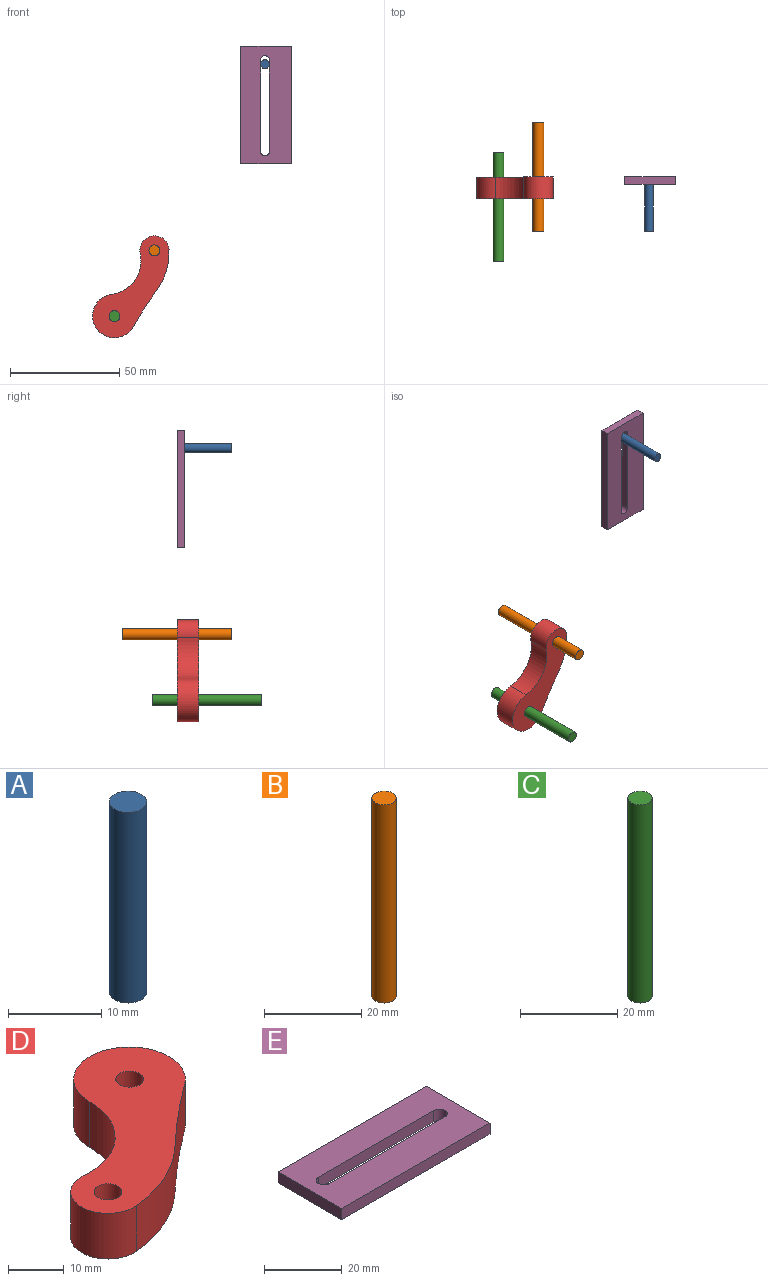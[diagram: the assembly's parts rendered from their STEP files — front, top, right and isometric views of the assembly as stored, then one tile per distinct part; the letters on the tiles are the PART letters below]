
ASSEMBLY  parts=5 mates=4
PART A: 3 faces, bbox 4x4x25 mm
  f0: cylinder r=2mm len=25mm, axis (0,0,-1), area 314.2mm2, adj f1,f2
  f1: plane 4x4mm, normal (0,0,1), area 12.6mm2, adj f0
  f2: plane 4x4mm, normal (0,0,-1), area 12.6mm2, adj f0
PART B: 3 faces, bbox 5x5x50 mm
  f0: cylinder r=2.5mm len=50mm, axis (0,0,-1), area 785.4mm2, adj f1,f2
  f1: plane 5x5mm, normal (0,0,1), area 19.6mm2, adj f0
  f2: plane 5x5mm, normal (0,0,-1), area 19.6mm2, adj f0
PART C: 3 faces, bbox 5x5x50 mm
  f0: cylinder r=2.5mm len=50mm, axis (0,0,-1), area 785.4mm2, adj f1,f2
  f1: plane 5x5mm, normal (0,0,1), area 19.6mm2, adj f0
  f2: plane 5x5mm, normal (0,0,-1), area 19.6mm2, adj f0
PART D: 9 faces, bbox 44.1x38.7x10 mm
  f0: cylinder r=10mm len=20mm, axis (0,0,-1), area 408.1mm2, adj f1,f5,f7,f8
  f1: cylinder r=15.41mm len=16.82mm, axis (0,0,-1), area 256.1mm2, adj f0,f2,f7,f8
  f2: cylinder r=6.67mm len=13.34mm, axis (0,0,-1), area 221.8mm2, adj f1,f3,f7,f8
  f3: cylinder r=29.75mm len=17.8mm, axis (0,0,-1), area 199.1mm2, adj f2,f5,f7,f8
  f4: cylinder r=2.5mm len=10mm, axis (0,0,-1), area 157.1mm2, adj f7,f8
  f5: cylinder r=150.72mm len=14.93mm, axis (0,0,-1), area 194.7mm2, adj f0,f3,f7,f8
  f6: cylinder r=2.5mm len=10mm, axis (0,0,-1), area 157.1mm2, adj f7,f8
  f7: plane 44.1x38.66mm, normal (0,0,1), area 679.5mm2, adj f0,f1,f2,f3,f4,f5,f6
  f8: plane 44.1x38.66mm, normal (0,0,-1), area 679.5mm2, adj f0,f1,f2,f3,f4,f5,f6
PART E: 10 faces, bbox 53.9x23.1x3.5 mm
  f0: cylinder r=2mm len=4mm, axis (0,0,-1), area 22mm2, adj f1,f7,f8,f9
  f1: plane 41.94x3.5mm, normal (0,-1,0), area 146.8mm2, adj f0,f2,f8,f9
  f2: cylinder r=2mm len=4mm, axis (0,0,-1), area 22mm2, adj f1,f7,f8,f9
  f3: plane 53.89x3.5mm, normal (0,1,0), area 188.6mm2, adj f4,f6,f8,f9
  f4: plane 23.14x3.5mm, normal (-1,0,0), area 81mm2, adj f3,f5,f8,f9
  f5: plane 53.89x3.5mm, normal (0,-1,0), area 188.6mm2, adj f4,f6,f8,f9
  f6: plane 23.14x3.5mm, normal (1,0,0), area 81mm2, adj f3,f5,f8,f9
  f7: plane 41.94x3.5mm, normal (0,1,0), area 146.8mm2, adj f0,f2,f8,f9
  f8: plane 53.89x23.14mm, normal (0,0,1), area 1066.7mm2, adj f0,f1,f2,f3,f4,f5,f6,f7
  f9: plane 53.89x23.14mm, normal (0,0,-1), area 1066.7mm2, adj f0,f1,f2,f3,f4,f5,f6,f7
PLACE A rot(axis=(0.96,-0.19,0.19),92.3deg) t=(50.7,0,97.99)mm
PLACE B rot(axis=(-0.47,0.62,0.62),129.6deg) t=(1.64,-10,-2.36)mm
PLACE C rot(axis=(-0.63,0.55,0.55),115.9deg) t=(5.88,-23.69,-31.31)mm
PLACE D rot(axis=(-0.63,0.55,0.55),115.9deg) t=(-0.01,-10,0.04)mm
PLACE E rot(axis=(0.58,-0.58,0.58),120deg) t=(55.49,0,58.75)mm fixed
MATE pin_slot A.f0 <-> E.f0  axis (0,1,0) through (68.88,0,115.31)mm
MATE slider C.f0 <-> D.f4  axis (0,-1,0) through (0,-13.69,0)mm
MATE planar D.f7 <-> E.f9  axis (0,1,0) through (8.75,0,10.86)mm
MATE revolute B.f0 <-> D.f2  axis (0,-1,0) through (18.3,0,30.05)mm
